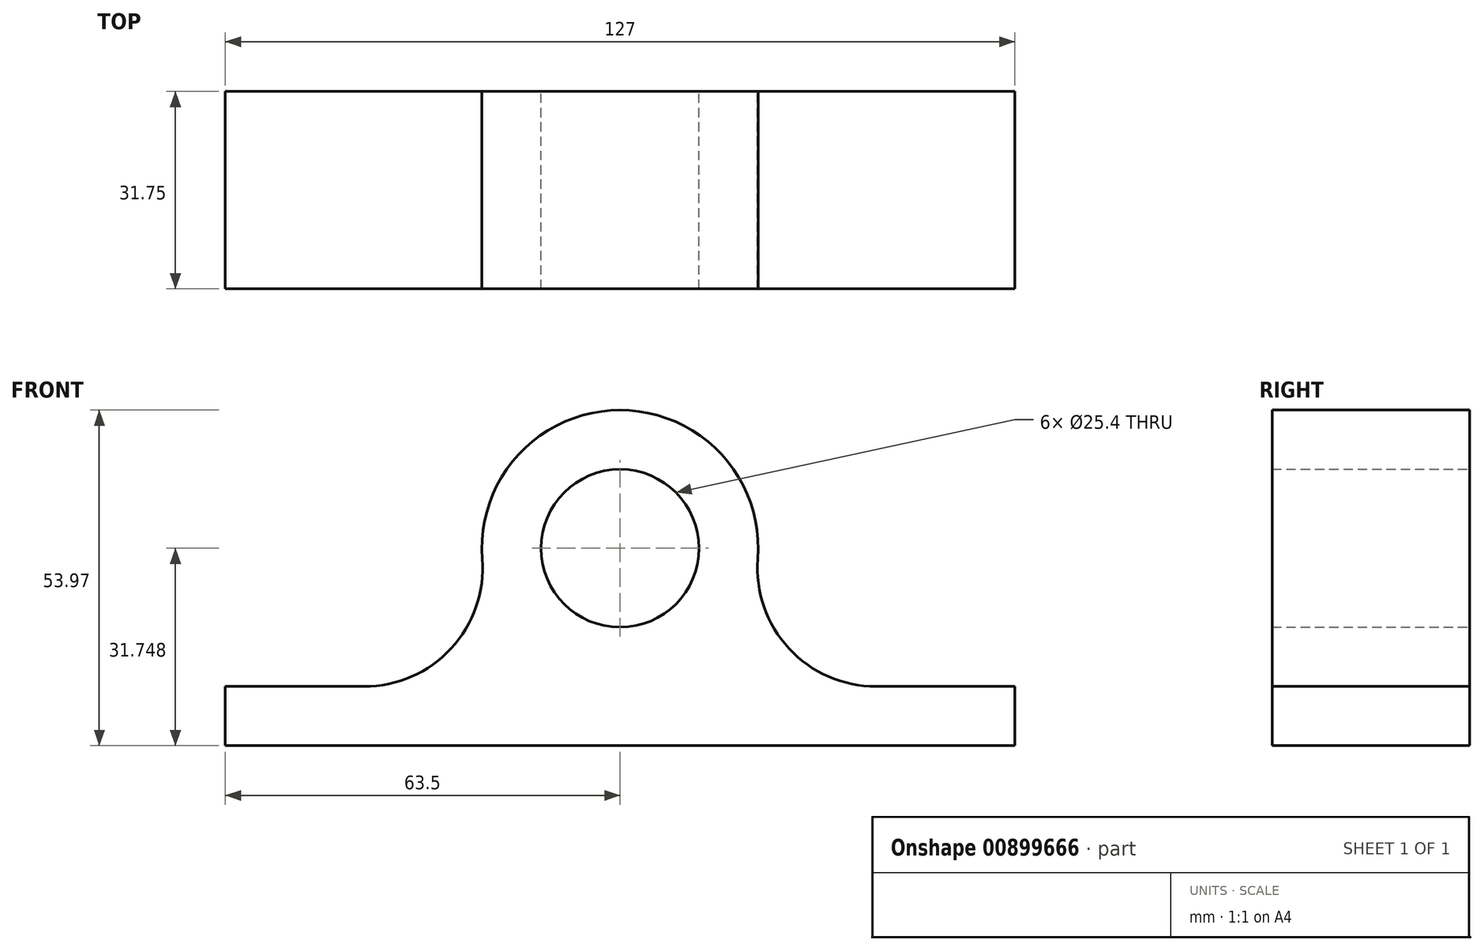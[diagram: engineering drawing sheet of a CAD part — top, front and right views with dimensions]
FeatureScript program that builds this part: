
annotation { "Feature Type Name" : "Feature", "Feature Type Description" : "" }
export const myFeature = defineFeature(function(context is Context, id is Id, definition is map)
    precondition{}
    {
        {
            var Q0;
            Q0=qCreatedBy(makeId("Front.planeOp"),FACE);
            var sketch = newSketch(context, id + "F0", { "sketchPlane" : qUnion([Q0])});
            skLineSegment(sketch, "E0.bottom", {"start": v(63.5, 4.76) * mm, "end": v(-63.5, 4.76) * mm});
            skLineSegment(sketch, "E0.top", {"start": v(63.5, -4.76) * mm, "end": v(-63.5, -4.76) * mm});
            skLineSegment(sketch, "E0.left", {"start": v(63.5, 4.76) * mm, "end": v(63.5, -4.76) * mm});
            skLineSegment(sketch, "E0.right", {"start": v(-63.5, 4.76) * mm, "end": v(-63.5, -4.76) * mm});
            skPoint(sketch, "E0.middle", {"position": v(0, 0) * mm});
            skCircle(sketch, "E1", {"center": v(0, 26.99) * mm, "radius": 12.7 * mm});
            skCircle(sketch, "E2", {"center": v(0, 26.99) * mm, "radius": 22.22 * mm});
            skCircle(sketch, "E3", {"center": v(41.15, 23.81) * mm, "radius": 19.05 * mm});
            skCircle(sketch, "E4", {"center": v(-41.15, 23.81) * mm, "radius": 19.05 * mm});
            skSolve(sketch);
        }
        {
            var Q0;
            Q0=makeQuery(id+"F0.imprint","IMPRINT",FACE,{"disambiguationData":[TD([[makeQuery(id+"F0.imprint","IMPRINT",EDGE,{"derivedFrom":sQuery(id+"F0.wireOp",EDGE,"E0.top")}),-1.0]])]});
            var Q1;
            {var subQ0=sQuery(id+"F0.wireOp",EDGE,"E3");var subQ1=sQuery(id+"F0.wireOp",EDGE,"E0.bottom");var subQ2=makeQuery(id+"F0.imprint","INTERSECT",VERTEX,{"derivedFrom":[subQ1,subQ0]});Q1=makeQuery(id+"F0.imprint","IMPRINT",FACE,{"disambiguationData":[TD([[makeQuery(id+"F0.imprint","IMPRINT",EDGE,{"disambiguationData":[TD([[subQ2,-1.0]])],"derivedFrom":subQ1}),-1.0]])]});}
            var Q2;
            {var subQ0=sQuery(id+"F0.wireOp",EDGE,"E4");var subQ1=sQuery(id+"F0.wireOp",EDGE,"E0.bottom");var subQ2=makeQuery(id+"F0.imprint","INTERSECT",VERTEX,{"derivedFrom":[subQ1,subQ0]});Q2=makeQuery(id+"F0.imprint","IMPRINT",FACE,{"disambiguationData":[TD([[makeQuery(id+"F0.imprint","IMPRINT",EDGE,{"disambiguationData":[TD([[subQ2,1.0]])],"derivedFrom":subQ1}),-1.0]])]});}
            var Q3;
            Q3=makeQuery(id+"F0.imprint","IMPRINT",FACE,{"disambiguationData":[TD([[makeQuery(id+"F0.imprint","IMPRINT",EDGE,{"derivedFrom":sQuery(id+"F0.wireOp",EDGE,"E1")}),-1.0]])]});
            extrude(context, id + "F1", {"entities" : qUnion([Q0, Q1, Q2, Q3]), "depth" : 31.75 * mm, "offsetDistance" : 25.4 * mm});
        }
    });
